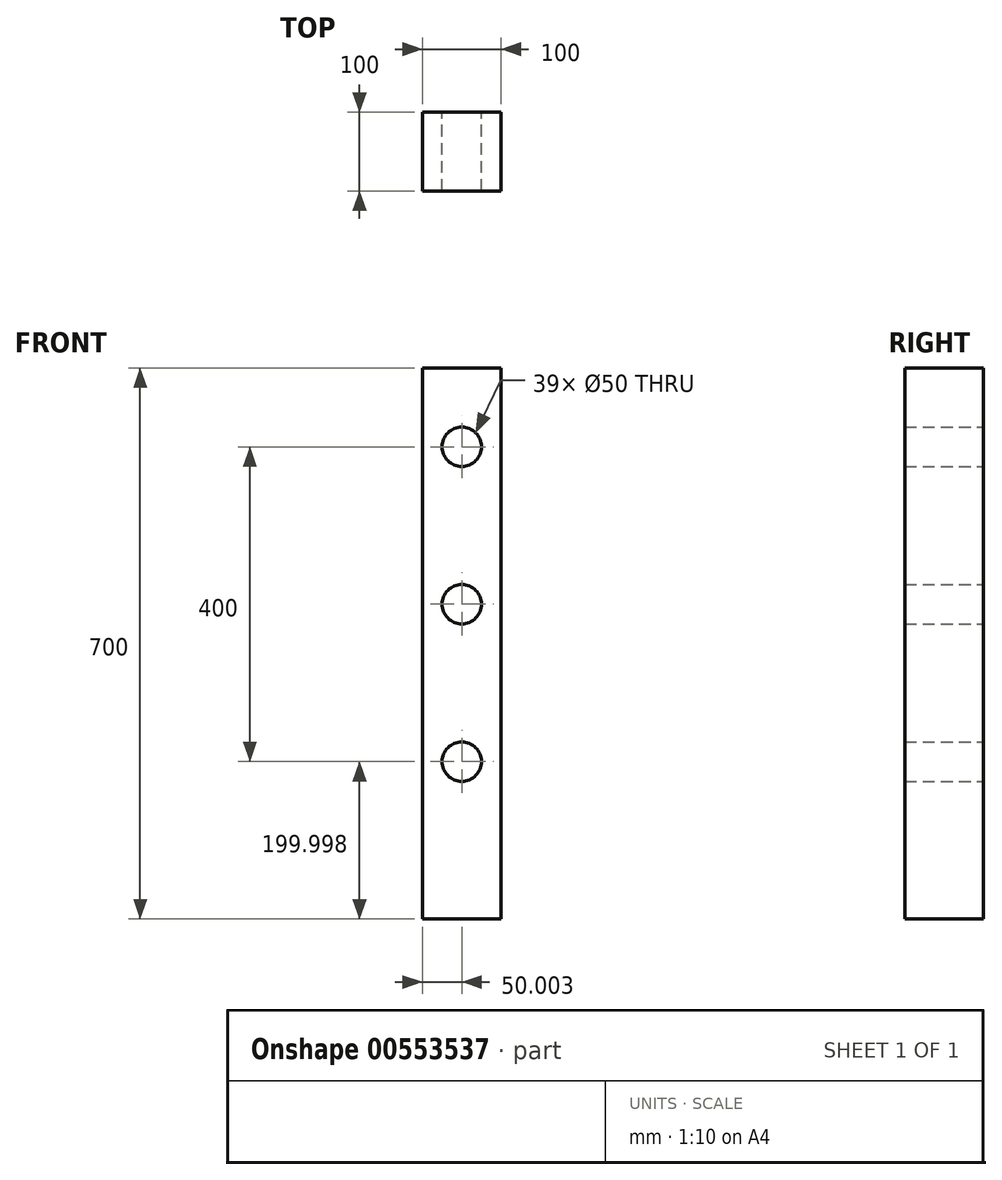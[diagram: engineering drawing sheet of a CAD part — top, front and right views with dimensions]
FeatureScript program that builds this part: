
annotation { "Feature Type Name" : "Feature", "Feature Type Description" : "" }
export const myFeature = defineFeature(function(context is Context, id is Id, definition is map)
    precondition{}
    {
        {
            var Q0;
            Q0=qCreatedBy(makeId("Front.planeOp"),FACE);
            var sketch = newSketch(context, id + "F0", { "sketchPlane" : qUnion([Q0])});
            skLineSegment(sketch, "E0.bottom", {"start": v(-554.02, 516.9) * mm, "end": v(-454.02, 516.9) * mm});
            skLineSegment(sketch, "E0.top", {"start": v(-554.02, -183.1) * mm, "end": v(-454.02, -183.1) * mm});
            skLineSegment(sketch, "E0.left", {"start": v(-554.02, 516.9) * mm, "end": v(-554.02, -183.1) * mm});
            skLineSegment(sketch, "E0.right", {"start": v(-454.02, 516.9) * mm, "end": v(-454.02, -183.1) * mm});
            skCircle(sketch, "E1", {"center": v(-504.02, 16.9) * mm, "radius": 25 * mm});
            skCircle(sketch, "E2", {"center": v(-504.02, 216.9) * mm, "radius": 25 * mm});
            skCircle(sketch, "E3", {"center": v(-504.02, 416.9) * mm, "radius": 25 * mm});
            skSolve(sketch);
        }
        {
            var Q0;
            Q0 = qSketchRegion(id + "F0", true);
            extrude(context, id + "F1", {"entities" : qUnion([Q0]), "depth" : 100 * mm, "offsetDistance" : 25 * mm});
        }
    });
